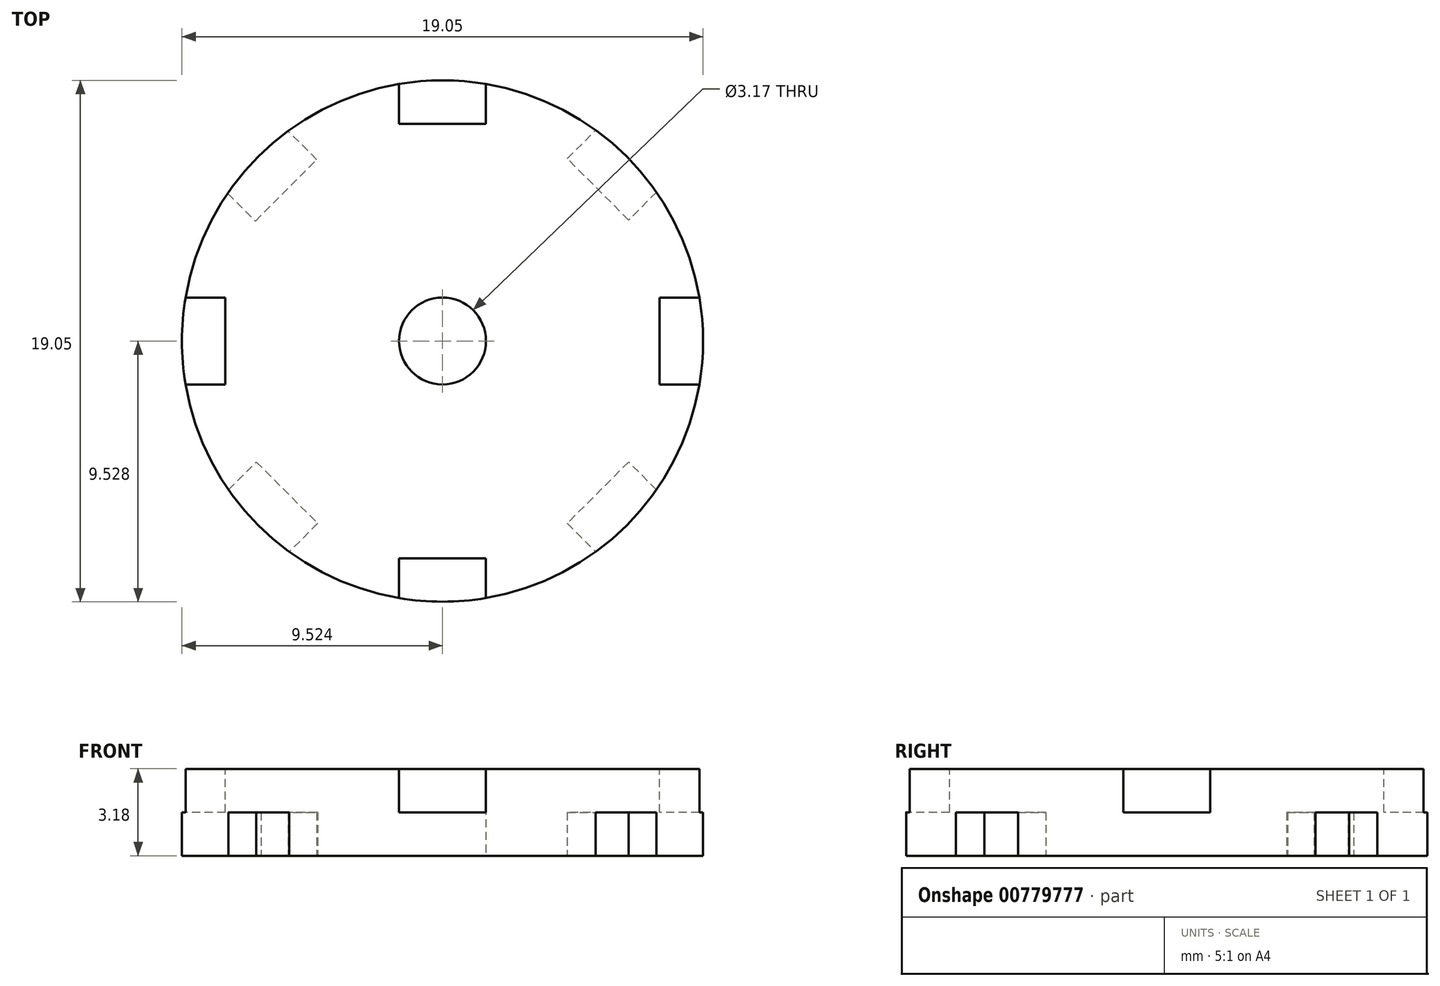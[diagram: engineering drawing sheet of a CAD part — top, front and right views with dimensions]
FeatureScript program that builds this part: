
annotation { "Feature Type Name" : "Feature", "Feature Type Description" : "" }
export const myFeature = defineFeature(function(context is Context, id is Id, definition is map)
    precondition{}
    {
        {
            var Q0;
            Q0=qCreatedBy(makeId("Top.planeOp"),FACE);
            var sketch = newSketch(context, id + "F0", { "sketchPlane" : qUnion([Q0])});
            skCircle(sketch, "E0", {"center": v(6.08, 0.92) * mm, "radius": 1.59 * mm});
            skCircle(sketch, "E1", {"center": v(6.08, 0.92) * mm, "radius": 9.53 * mm});
            skSolve(sketch);
        }
        {
            var Q0;
            Q0=makeQuery(id+"F0.imprint","IMPRINT",FACE,{"disambiguationData":[TD([[makeQuery(id+"F0.imprint","IMPRINT",EDGE,{"derivedFrom":sQuery(id+"F0.wireOp",EDGE,"E0")}),-1.0]])]});
            extrude(context, id + "F1", {"entities" : qUnion([Q0]), "depth" : 3.17 * mm, "offsetDistance" : 25.4 * mm});
        }
        {
            var Q0;
            Q0=makeQuery(id+"F1.opExtrude","CAP_FACE",FACE,{"disambiguationData":[OSD([sQuery(id+"F0.wireOp",EDGE,"E0"),sQuery(id+"F0.wireOp",EDGE,"E1")])],"isStart":false});
            var sketch = newSketch(context, id + "F2", { "sketchPlane" : qUnion([Q0])});
            skLineSegment(sketch, "E2.bottom", {"start": v(4.5, 10.44) * mm, "end": v(7.67, 10.44) * mm});
            skLineSegment(sketch, "E2.top", {"start": v(4.5, 8.86) * mm, "end": v(7.67, 8.86) * mm});
            skLineSegment(sketch, "E2.left", {"start": v(4.5, 10.44) * mm, "end": v(4.5, 8.86) * mm});
            skLineSegment(sketch, "E2.right", {"start": v(7.67, 10.44) * mm, "end": v(7.67, 8.86) * mm});
            skLineSegment(sketch, "E3.bottom", {"start": v(15.6, 2.5) * mm, "end": v(14.02, 2.5) * mm});
            skLineSegment(sketch, "E3.top", {"start": v(15.6, -0.67) * mm, "end": v(14.02, -0.67) * mm});
            skLineSegment(sketch, "E3.left", {"start": v(15.6, 2.5) * mm, "end": v(15.6, -0.67) * mm});
            skLineSegment(sketch, "E3.right", {"start": v(14.02, 2.5) * mm, "end": v(14.02, -0.67) * mm});
            skLineSegment(sketch, "E4.bottom", {"start": v(7.67, -7.02) * mm, "end": v(4.5, -7.02) * mm});
            skLineSegment(sketch, "E4.top", {"start": v(7.67, -8.6) * mm, "end": v(4.5, -8.6) * mm});
            skLineSegment(sketch, "E4.left", {"start": v(7.67, -7.02) * mm, "end": v(7.67, -8.6) * mm});
            skLineSegment(sketch, "E4.right", {"start": v(4.5, -7.02) * mm, "end": v(4.5, -8.6) * mm});
            skLineSegment(sketch, "E5.bottom", {"start": v(-1.85, -0.67) * mm, "end": v(-3.44, -0.67) * mm});
            skLineSegment(sketch, "E5.top", {"start": v(-1.85, 2.5) * mm, "end": v(-3.44, 2.5) * mm});
            skLineSegment(sketch, "E5.left", {"start": v(-1.85, -0.67) * mm, "end": v(-1.85, 2.5) * mm});
            skLineSegment(sketch, "E5.right", {"start": v(-3.44, -0.67) * mm, "end": v(-3.44, 2.5) * mm});
            skSolve(sketch);
        }
        {
            var Q0;
            {var subQ5=sQuery(id+"F2.wireOp",EDGE,"E2.top");Q0=makeQuery(id+"F2.imprint","IMPRINT",FACE,{"disambiguationData":[TD([[makeQuery(id+"F2.imprint","IMPRINT",EDGE,{"derivedFrom":subQ5}),1.0]])]});}
            var Q1;
            {var subQ4=sQuery(id+"F2.wireOp",EDGE,"E5.left");Q1=makeQuery(id+"F2.imprint","IMPRINT",FACE,{"disambiguationData":[TD([[makeQuery(id+"F2.imprint","IMPRINT",EDGE,{"derivedFrom":subQ4}),1.0]])]});}
            var Q2;
            {var subQ4=sQuery(id+"F2.wireOp",EDGE,"E4.bottom");Q2=makeQuery(id+"F2.imprint","IMPRINT",FACE,{"disambiguationData":[TD([[makeQuery(id+"F2.imprint","IMPRINT",EDGE,{"derivedFrom":subQ4}),1.0]])]});}
            var Q3;
            {var subQ4=sQuery(id+"F2.wireOp",EDGE,"E3.right");Q3=makeQuery(id+"F2.imprint","IMPRINT",FACE,{"disambiguationData":[TD([[makeQuery(id+"F2.imprint","IMPRINT",EDGE,{"derivedFrom":subQ4}),1.0]])]});}
            extrude(context, id + "F3", {"entities" : qUnion([Q0, Q1, Q2, Q3]), "operationType" : NewBodyOperationType.REMOVE, "oppositeDirection" : true, "depth" : 1.59 * mm, "offsetDistance" : 25.4 * mm});
        }
        {
            var Q0;
            Q0=makeQuery(id+"F1.opExtrude","CAP_FACE",FACE,{"disambiguationData":[OSD([sQuery(id+"F0.wireOp",EDGE,"E0"),sQuery(id+"F0.wireOp",EDGE,"E1")])],"isStart":true});
            var sketch = newSketch(context, id + "F4", { "sketchPlane" : qUnion([Q0])});
            skLineSegment(sketch, "E6", {"start": v(-1.84, 4.62) * mm, "end": v(-0.72, 3.5) * mm});
            skLineSegment(sketch, "E7", {"start": v(-0.72, 3.5) * mm, "end": v(1.52, 5.75) * mm});
            skLineSegment(sketch, "E8", {"start": v(1.52, 5.75) * mm, "end": v(0.4, 6.87) * mm});
            skLineSegment(sketch, "E9", {"start": v(0.4, 6.87) * mm, "end": v(-1.84, 4.62) * mm});
            skLineSegment(sketch, "E10", {"start": v(-0.76, -7.55) * mm, "end": v(-1.88, -6.42) * mm});
            skLineSegment(sketch, "E11", {"start": v(-1.88, -6.42) * mm, "end": v(-0.76, -5.3) * mm});
            skLineSegment(sketch, "E12", {"start": v(-0.76, -5.3) * mm, "end": v(1.49, -7.55) * mm});
            skLineSegment(sketch, "E13", {"start": v(1.49, -7.55) * mm, "end": v(0.37, -8.67) * mm});
            skLineSegment(sketch, "E14", {"start": v(0.37, -8.67) * mm, "end": v(-0.76, -7.55) * mm});
            skLineSegment(sketch, "E15", {"start": v(11.77, -8.7) * mm, "end": v(14.01, -6.46) * mm});
            skLineSegment(sketch, "E16", {"start": v(14.01, -6.46) * mm, "end": v(12.89, -5.34) * mm});
            skLineSegment(sketch, "E17", {"start": v(12.89, -5.34) * mm, "end": v(10.64, -7.58) * mm});
            skLineSegment(sketch, "E18", {"start": v(10.64, -7.58) * mm, "end": v(11.77, -8.7) * mm});
            skLineSegment(sketch, "E19", {"start": v(10.64, 5.75) * mm, "end": v(11.77, 6.87) * mm});
            skLineSegment(sketch, "E20", {"start": v(11.77, 6.87) * mm, "end": v(14.01, 4.62) * mm});
            skLineSegment(sketch, "E21", {"start": v(14.01, 4.62) * mm, "end": v(12.89, 3.5) * mm});
            skLineSegment(sketch, "E22", {"start": v(12.89, 3.5) * mm, "end": v(10.64, 5.75) * mm});
            skSolve(sketch);
        }
        {
            var Q0;
            {var subQ1=sQuery(id+"F4.wireOp",EDGE,"E7");Q0=makeQuery(id+"F4.imprint","IMPRINT",FACE,{"disambiguationData":[TD([[makeQuery(id+"F4.imprint","IMPRINT",EDGE,{"derivedFrom":subQ1}),1.0]])]});}
            var Q1;
            {var subQ4=sQuery(id+"F4.wireOp",EDGE,"E22");Q1=makeQuery(id+"F4.imprint","IMPRINT",FACE,{"disambiguationData":[TD([[makeQuery(id+"F4.imprint","IMPRINT",EDGE,{"derivedFrom":subQ4}),-1.0]])]});}
            var Q2;
            {var subQ1=sQuery(id+"F4.wireOp",EDGE,"E17");Q2=makeQuery(id+"F4.imprint","IMPRINT",FACE,{"disambiguationData":[TD([[makeQuery(id+"F4.imprint","IMPRINT",EDGE,{"derivedFrom":subQ1}),1.0]])]});}
            var Q3;
            {var subQ1=sQuery(id+"F4.wireOp",EDGE,"E12");Q3=makeQuery(id+"F4.imprint","IMPRINT",FACE,{"disambiguationData":[TD([[makeQuery(id+"F4.imprint","IMPRINT",EDGE,{"derivedFrom":subQ1}),-1.0]])]});}
            extrude(context, id + "F5", {"entities" : qUnion([Q0, Q1, Q2, Q3]), "operationType" : NewBodyOperationType.REMOVE, "oppositeDirection" : true, "depth" : 1.59 * mm, "offsetDistance" : 25.4 * mm});
        }
    });
